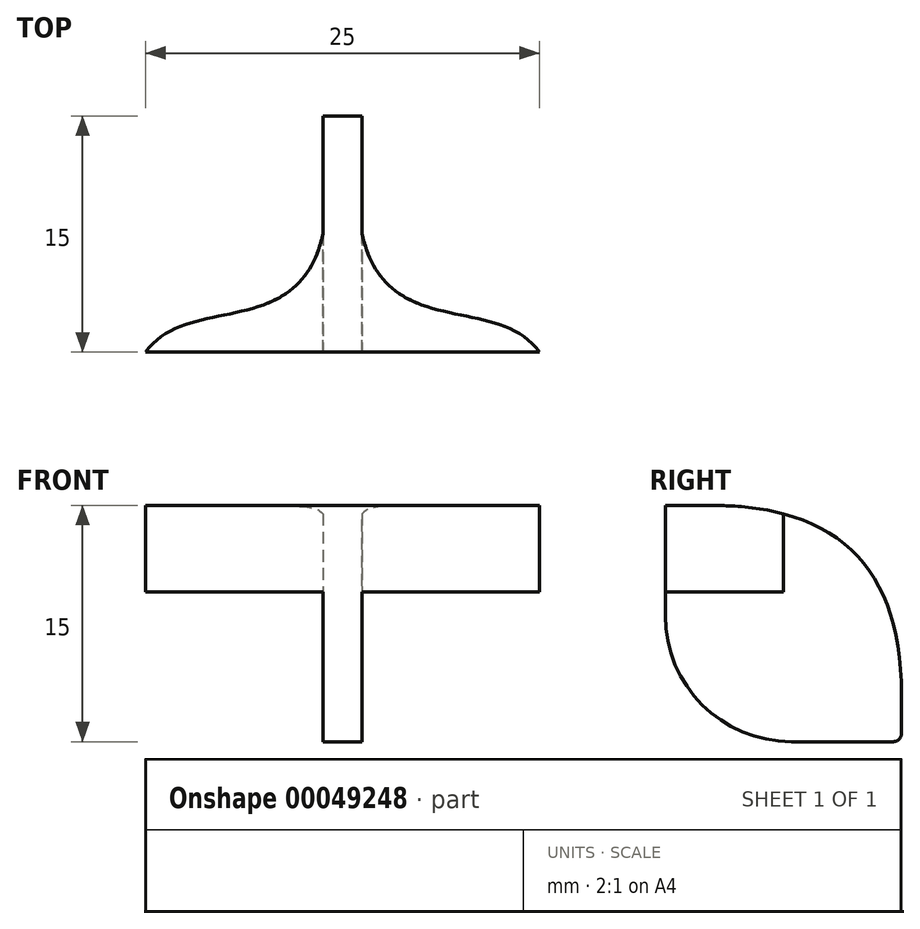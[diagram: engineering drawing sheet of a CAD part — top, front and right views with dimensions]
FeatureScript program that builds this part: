
annotation { "Feature Type Name" : "Feature", "Feature Type Description" : "" }
export const myFeature = defineFeature(function(context is Context, id is Id, definition is map)
    precondition{}
    {
        {
            var Q0;
            Q0=qCreatedBy(makeId("Top.planeOp"),FACE);
            var sketch = newSketch(context, id + "F0", { "sketchPlane" : qUnion([Q0])});
            skLineSegment(sketch, "E0.bottom", {"start": v(-1.25, 7.5) * mm, "end": v(1.25, 7.5) * mm});
            skLineSegment(sketch, "E0.top", {"start": v(-1.25, -7.5) * mm, "end": v(1.25, -7.5) * mm});
            skLineSegment(sketch, "E0.left", {"start": v(-1.25, 7.5) * mm, "end": v(-1.25, -7.5) * mm});
            skLineSegment(sketch, "E0.right", {"start": v(1.25, 7.5) * mm, "end": v(1.25, -7.5) * mm});
            skPoint(sketch, "E0.middle", {"position": v(0, 0) * mm});
            skSolve(sketch);
        }
        {
            var Q0;
            Q0=makeQuery(id+"F0.imprint","IMPRINT",FACE,{"disambiguationData":[TD([[makeQuery(id+"F0.imprint","IMPRINT",EDGE,{"derivedFrom":sQuery(id+"F0.wireOp",EDGE,"E0.bottom")}),-1.0]])]});
            extrude(context, id + "F1", {"entities" : qUnion([Q0]), "depth" : 15 * mm});
        }
        {
            var Q0;
            Q0=qCreatedBy(makeId("Front.planeOp"),FACE);
            var sketch = newSketch(context, id + "F2", { "sketchPlane" : qUnion([Q0])});
            skLineSegment(sketch, "E1.bottom", {"start": v(-12.5, 15) * mm, "end": v(12.5, 15) * mm});
            skLineSegment(sketch, "E1.top", {"start": v(-12.5, 9.5) * mm, "end": v(12.5, 9.5) * mm});
            skLineSegment(sketch, "E1.left", {"start": v(-12.5, 15) * mm, "end": v(-12.5, 9.5) * mm});
            skLineSegment(sketch, "E1.right", {"start": v(12.5, 15) * mm, "end": v(12.5, 9.5) * mm});
            skLineSegment(sketch, "E2", {"start": v(0, 19.49) * mm, "end": v(0, 10.51) * mm, "construction": true});
            skLineSegment(sketch, "E3.0", {"start": v(-1.25, 15) * mm, "end": v(1.25, 15) * mm});
            skSolve(sketch);
        }
        {
            var Q0;
            Q0=makeQuery(id+"F2.imprint","IMPRINT",FACE,{"disambiguationData":[TD([[makeQuery(id+"F2.imprint","IMPRINT",EDGE,{"derivedFrom":sQuery(id+"F2.wireOp",EDGE,"E1.top")}),1.0]])]});
            var Q1;
            Q1=makeQuery(id+"F1.opExtrude","SWEPT_FACE",FACE,{"disambiguationData":[OSD([sQuery(id+"F0.wireOp",EDGE,"E0.top")])]});
            extrude(context, id + "F3", {"entities" : qUnion([Q0]), "operationType" : NewBodyOperationType.ADD, "endBound" : BoundingType.UP_TO_SURFACE, "endBoundEntityFace" : qUnion([Q1]), "depth" : 25 * mm});
        }
        {
            var Q0;
            Q0=makeQuery(id+"F1.opExtrude","CAP_EDGE",EDGE,{"disambiguationData":[OSD([sQuery(id+"F0.wireOp",EDGE,"E0.bottom")])],"isStart":false});
            fillet(context, id + "F4", {"entities" : qUnion([Q0]), "radius" : 12 * mm, "tangentPropagation" : true, "rho" : 0.5, "crossSection" : FilletCrossSection.CONIC, "allowEdgeOverflow" : false});
        }
        {
            var Q0;
            Q0=makeQuery(id+"F3.opExtrude","CAP_EDGE",EDGE,{"disambiguationData":[OSD([sQuery(id+"F2.wireOp",EDGE,"E1.left")])],"isStart":true});
            var Q1;
            Q1=makeQuery(id+"F3.opExtrude","CAP_EDGE",EDGE,{"disambiguationData":[OSD([sQuery(id+"F2.wireOp",EDGE,"E1.right")])],"isStart":true});
            fillet(context, id + "F5", {"entities" : qUnion([Q0, Q1]), "radius" : 11.4 * mm, "tangentPropagation" : true, "allowEdgeOverflow" : false});
        }
        {
            var Q0;
            Q0=makeQuery(id+"F1.opExtrude","CAP_EDGE",EDGE,{"disambiguationData":[OSD([sQuery(id+"F0.wireOp",EDGE,"E0.bottom")])],"isStart":true});
            fillet(context, id + "F6", {"entities" : qUnion([Q0]), "radius" : 0.5 * mm, "tangentPropagation" : true, "allowEdgeOverflow" : false});
        }
        {
            var Q0;
            Q0=makeQuery(id+"F1.opExtrude","CAP_EDGE",EDGE,{"disambiguationData":[OSD([sQuery(id+"F0.wireOp",EDGE,"E0.top")])],"isStart":true});
            fillet(context, id + "F7", {"entities" : qUnion([Q0]), "radius" : 8 * mm, "tangentPropagation" : true, "allowEdgeOverflow" : false});
        }
        {
            var Q0;
            {var subQ3=sQuery(id+"F2.wireOp",EDGE,"E1.top");Q0=makeQuery(id+"F3.boolean.opBoolean","SPLIT",FACE,{"disambiguationData":[TD([makeQuery(id+"F1.opExtrude","SWEPT_FACE",FACE,{"disambiguationData":[OSD([sQuery(id+"F0.wireOp",EDGE,"E0.right")])]})])],"derivedFrom":makeQuery(id+"F3.opExtrude","SWEPT_FACE",FACE,{"disambiguationData":[OSD([subQ3])]})});}
            var sketch = newSketch(context, id + "F8", { "sketchPlane" : qUnion([Q0])});
            skLineSegment(sketch, "E4.0", {"start": v(12.5, 7.5) * mm, "end": v(1.25, 7.5) * mm});
            skArc(sketch, "E5.0", {"start": v(1.79, 0) * mm, "mid": v(8.33, 2.06) * mm, "end": v(12.5, 7.5) * mm});
            skLineSegment(sketch, "E6.0", {"start": v(1.25, 0) * mm, "end": v(1.25, 7.5) * mm});
            skLineSegment(sketch, "E7.0", {"start": v(1.25, 0) * mm, "end": v(1.79, 0) * mm});
            skArc(sketch, "E8.0", {"start": v(-12.5, 7.5) * mm, "mid": v(-8.33, 2.06) * mm, "end": v(-1.79, 0) * mm});
            skLineSegment(sketch, "E9.0", {"start": v(-1.79, 0) * mm, "end": v(-1.25, 0) * mm});
            skLineSegment(sketch, "E10.0", {"start": v(-1.25, 0) * mm, "end": v(-1.25, 7.5) * mm});
            skLineSegment(sketch, "E11.0", {"start": v(-1.25, 7.5) * mm, "end": v(-12.5, 7.5) * mm});
            skFitSpline(sketch, "E12", {"points": [v(1.25, 0) * mm, v(12.5, 7.5) * mm], "startDerivative": vector(4.42, 20.59) * mm, "endDerivative": vector(8.17, 11.34) * mm});
            skLineSegment(sketch, "E13", {"start": v(0, 0.47) * mm, "end": v(0, -0.65) * mm, "construction": true});
            skFitSpline(sketch, "E14.MirrorCS", {"points": [v(-1.25, 0) * mm, v(-12.5, 7.5) * mm], "startDerivative": vector(-4.42, 20.59) * mm, "endDerivative": vector(-8.17, 11.34) * mm});
            skSolve(sketch);
        }
        {
            var Q0;
            Q0=makeQuery(id+"F8.imprint","IMPRINT",FACE,{"disambiguationData":[TD([[makeQuery(id+"F8.imprint","IMPRINT",EDGE,{"derivedFrom":sQuery(id+"F8.wireOp",EDGE,"E5.0")}),1.0]])]});
            var Q1;
            Q1=makeQuery(id+"F8.imprint","IMPRINT",FACE,{"disambiguationData":[TD([[makeQuery(id+"F8.imprint","IMPRINT",EDGE,{"derivedFrom":sQuery(id+"F8.wireOp",EDGE,"E8.0")}),1.0]])]});
            extrude(context, id + "F9", {"entities" : qUnion([Q0, Q1]), "operationType" : NewBodyOperationType.REMOVE, "oppositeDirection" : true, "depth" : 25 * mm});
        }
    });
